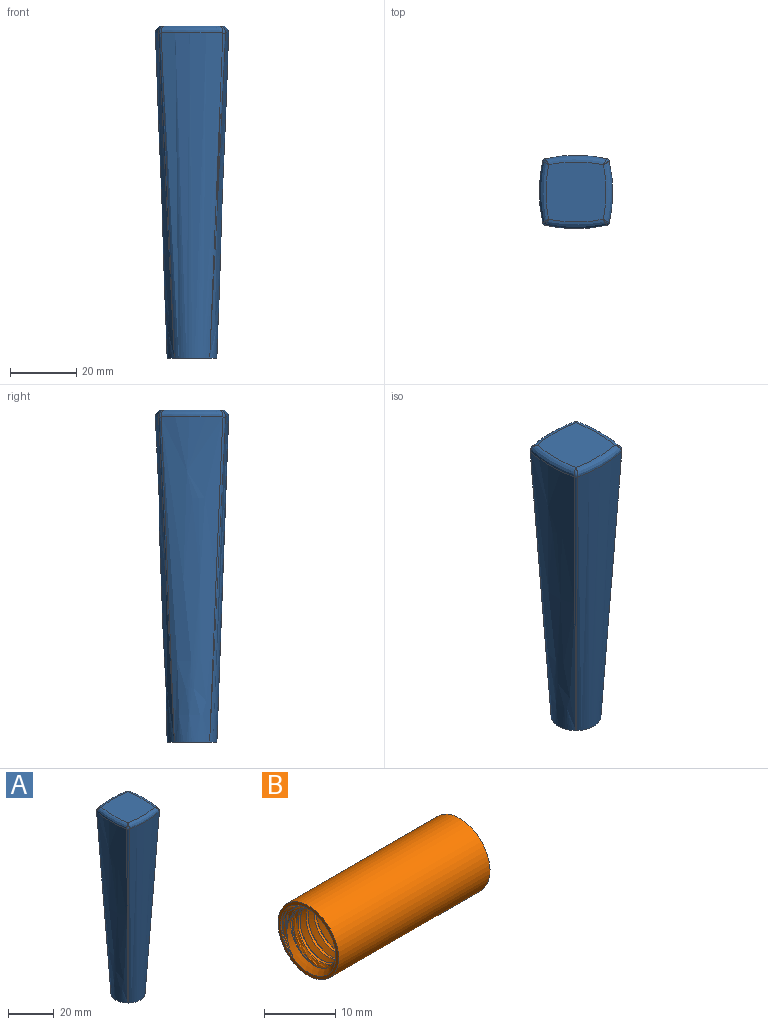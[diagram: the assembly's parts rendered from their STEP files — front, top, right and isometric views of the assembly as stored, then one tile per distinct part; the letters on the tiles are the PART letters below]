
ASSEMBLY  parts=2 mates=1
PART A: 20 faces, bbox 22.3x22.3x112.9 mm
  f0: plane 18.1x18.1mm, normal (0,0,1), area 306.9mm2, adj f6,f7,f8,f9
  f1: plane 15x15mm, normal (0,0,-1), area 63.6mm2, adj f2,f3,f4,f5,f18
  f2: bspline ~100x20mm, area 1490.8mm2, adj f1,f8,f10,f14
  f3: bspline ~100x20mm, area 1490.8mm2, adj f1,f6,f10,f12
  f4: bspline ~100x20mm, area 1490.8mm2, adj f1,f7,f12,f16
  f5: bspline ~100x20mm, area 1490.8mm2, adj f1,f9,f14,f16
  f6: bspline ~19.19x3.1mm, area 57.2mm2, adj f0,f3,f11,f13
  f7: bspline ~19.19x3.1mm, area 57.2mm2, adj f0,f4,f13,f17
  f8: bspline ~19.19x3.1mm, area 57.2mm2, adj f0,f2,f11,f15
  f9: bspline ~19.19x3.1mm, area 57.2mm2, adj f0,f5,f15,f17
  f10: bspline ~112.88x5.43mm, area 42.8mm2, adj f2,f3,f11
  f11: bspline ~2.29x1.82mm, area 1.7mm2, adj f6,f8,f10
  f12: bspline ~112.88x5.43mm, area 42.8mm2, adj f3,f4,f13
  f13: bspline ~2.29x1.82mm, area 1.7mm2, adj f6,f7,f12
  f14: bspline ~112.88x5.43mm, area 42.8mm2, adj f2,f5,f15
  f15: bspline ~2.29x1.82mm, area 1.7mm2, adj f8,f9,f14
  f16: bspline ~112.88x5.43mm, area 42.8mm2, adj f4,f5,f17
  f17: bspline ~2.29x1.82mm, area 1.7mm2, adj f7,f9,f16
  f18: cylinder r=6mm len=30mm, axis (0,0,-1), area 1131mm2, adj f1,f19
  f19: plane 12x12mm, normal (0,0,-1), area 113.1mm2, adj f18
PART B: 8 faces, bbox 31.7x13x12.5 mm
  f0: cylinder r=4.47mm len=29mm, axis (1,0,0), area 224.8mm2, adj f3,f5,f6,f7
  f1: cylinder r=6mm len=30mm, axis (1,0,0), area 1131mm2, adj f2,f3
  f2: plane 12x12mm, normal (-1,0,0), area 18.9mm2, adj f1,f7
  f3: plane 12.46x12.46mm, normal (1,0,0), area 38.7mm2, adj f0,f1,f4,f5,f6
  f4: bspline ~30.63x12.52mm, area 151.6mm2, adj f3,f5,f6,f7
  f5: bspline ~31.19x12.32mm, area 567mm2, adj f0,f3,f4,f7
  f6: bspline ~30.66x12.32mm, area 566.5mm2, adj f0,f3,f4,f7
  f7: cone r=5.47mm half-angle=45deg, axis (-1,0,0), area 27.9mm2, adj f0,f2,f4,f5,f6
PLACE A t=(1.71,-10.52,-15.51)mm
PLACE B rot(axis=(0,-1,0),90deg) t=(1.71,-10.52,14.49)mm
MATE fastened A.f18 <-> B.f1  axis (0,0,-1) through (1.71,-10.52,14.49)mm
